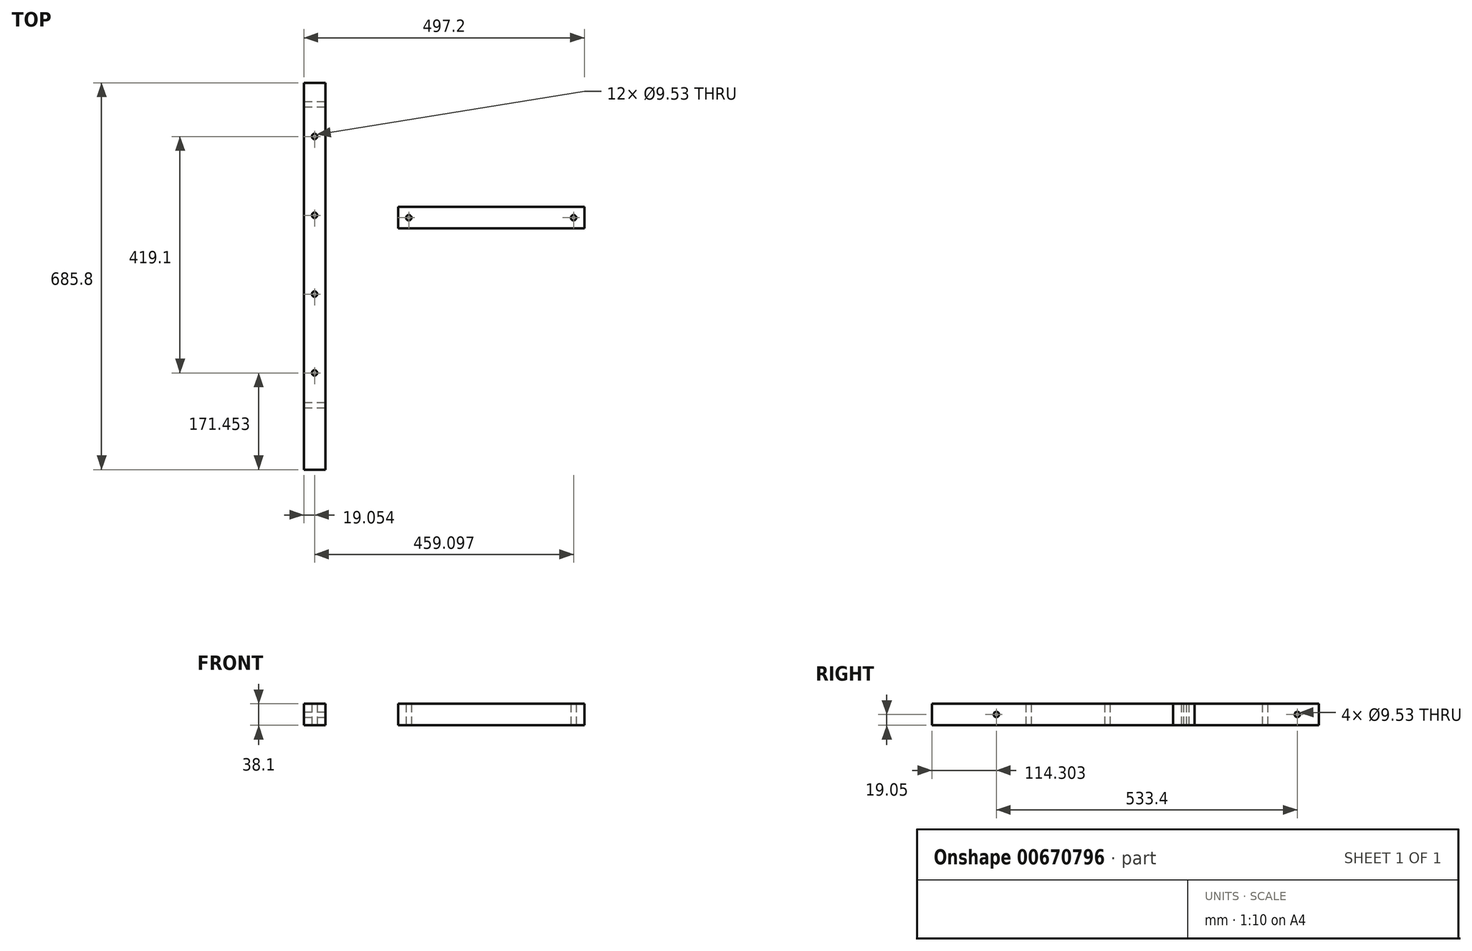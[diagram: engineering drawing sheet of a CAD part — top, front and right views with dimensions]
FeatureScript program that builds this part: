
annotation { "Feature Type Name" : "Feature", "Feature Type Description" : "" }
export const myFeature = defineFeature(function(context is Context, id is Id, definition is map)
    precondition{}
    {
        {
            var Q0;
            Q0=qCreatedBy(makeId("Top.planeOp"),FACE);
            var sketch = newSketch(context, id + "F0", { "sketchPlane" : qUnion([Q0])});
            skLineSegment(sketch, "E0.bottom", {"start": v(-17.74, 378.87) * mm, "end": v(20.36, 378.87) * mm});
            skLineSegment(sketch, "E0.top", {"start": v(-17.74, -306.93) * mm, "end": v(20.36, -306.93) * mm});
            skLineSegment(sketch, "E0.left", {"start": v(-17.74, 378.87) * mm, "end": v(-17.74, -306.93) * mm});
            skLineSegment(sketch, "E0.right", {"start": v(20.36, 378.87) * mm, "end": v(20.36, -306.93) * mm});
            skSolve(sketch);
        }
        {
            var Q0;
            Q0=makeQuery(id+"F0.imprint","IMPRINT",FACE,{"disambiguationData":[TD([[makeQuery(id+"F0.imprint","IMPRINT",EDGE,{"derivedFrom":sQuery(id+"F0.wireOp",EDGE,"E0.bottom")}),-1.0]])]});
            var Q1;
            Q1 = qSketchRegion(id + "F2", true);
            extrude(context, id + "F1", {"entities" : qUnion([Q0, Q1]), "depth" : 38.1 * mm, "offsetDistance" : 25.4 * mm});
        }
        {
            var Q0;
            Q0=makeQuery(id+"F1.opExtrude","CAP_FACE",FACE,{"disambiguationData":[OSD([sQuery(id+"F0.wireOp",EDGE,"E0.bottom"),sQuery(id+"F0.wireOp",EDGE,"E0.top"),sQuery(id+"F0.wireOp",EDGE,"E0.left"),sQuery(id+"F0.wireOp",EDGE,"E0.right")])],"isStart":true});
            var sketch = newSketch(context, id + "F2", { "sketchPlane" : qUnion([Q0])});
            skPoint(sketch, "E1", {"position": v(1.31, -283.62) * mm});
            skPoint(sketch, "E2", {"position": v(1.31, -143.92) * mm});
            skPoint(sketch, "E3", {"position": v(1.31, -4.22) * mm});
            skPoint(sketch, "E4", {"position": v(1.31, 135.48) * mm});
            skSolve(sketch);
        }
        {
            var Q0;
            Q0=makeQuery(id+"F1.opExtrude","SWEPT_FACE",FACE,{"disambiguationData":[OSD([sQuery(id+"F0.wireOp",EDGE,"E0.right")])]});
            var sketch = newSketch(context, id + "F3", { "sketchPlane" : qUnion([Q0])});
            skPoint(sketch, "E5", {"position": v(-192.63, 19.05) * mm});
            skPoint(sketch, "E6", {"position": v(340.77, 19.05) * mm});
            skSolve(sketch);
        }
        {
            var Q0;
            Q0=sQuery(id+"F2.wireOp",VERTEX,"a3873a67-aabc-4409-9fdf-016a4dbcbf0b");
            var Q1;
            Q1=sQuery(id+"F2.wireOp",VERTEX,"E4");
            var Q2;
            Q2=makeQuery(id+"F1.opExtrude","SWEPT_BODY",BODY,{"disambiguationData":[OSD([sQuery(id+"F0.wireOp",EDGE,"E0.bottom"),sQuery(id+"F0.wireOp",EDGE,"E0.top"),sQuery(id+"F0.wireOp",EDGE,"E0.left"),sQuery(id+"F0.wireOp",EDGE,"E0.right")])]});
            hole(context, id + "F4", {"style" : HoleStyle.SIMPLE, "endStyle" : HoleEndStyle.THROUGH, "holeDiameter" : 9.52 * mm, "majorDiameter" : 6.35 * mm, "isTappedThrough" : true, "tappedDepth" : 12.7 * mm, "tapClearance" : 3, "startFromSketch" : true, "locations" : qUnion([Q0, Q1]), "scope" : qUnion([Q2])});
        }
        {
            var Q0;
            Q0=sQuery(id+"F2.wireOp",VERTEX,"83af786d-4d35-481f-8a64-2c29215b7ae6");
            var Q1;
            Q1=sQuery(id+"F2.wireOp",VERTEX,"E3");
            var Q2;
            Q2=makeQuery(id+"F1.opExtrude","SWEPT_BODY",BODY,{"disambiguationData":[OSD([sQuery(id+"F0.wireOp",EDGE,"E0.bottom"),sQuery(id+"F0.wireOp",EDGE,"E0.top"),sQuery(id+"F0.wireOp",EDGE,"E0.left"),sQuery(id+"F0.wireOp",EDGE,"E0.right")])]});
            hole(context, id + "F5", {"style" : HoleStyle.SIMPLE, "endStyle" : HoleEndStyle.THROUGH, "holeDiameter" : 9.52 * mm, "majorDiameter" : 6.35 * mm, "isTappedThrough" : true, "tappedDepth" : 12.7 * mm, "tapClearance" : 3, "startFromSketch" : true, "locations" : qUnion([Q0, Q1]), "scope" : qUnion([Q2])});
        }
        {
            var Q0;
            Q0=sQuery(id+"F2.wireOp",VERTEX,"d702d4f4-6dca-422e-905c-935ee7591422");
            var Q1;
            Q1=sQuery(id+"F2.wireOp",VERTEX,"E2");
            var Q2;
            Q2=makeQuery(id+"F1.opExtrude","SWEPT_BODY",BODY,{"disambiguationData":[OSD([sQuery(id+"F0.wireOp",EDGE,"E0.bottom"),sQuery(id+"F0.wireOp",EDGE,"E0.top"),sQuery(id+"F0.wireOp",EDGE,"E0.left"),sQuery(id+"F0.wireOp",EDGE,"E0.right")])]});
            hole(context, id + "F6", {"style" : HoleStyle.SIMPLE, "endStyle" : HoleEndStyle.THROUGH, "holeDiameter" : 9.52 * mm, "majorDiameter" : 6.35 * mm, "isTappedThrough" : true, "tappedDepth" : 12.7 * mm, "tapClearance" : 3, "startFromSketch" : true, "locations" : qUnion([Q0, Q1]), "scope" : qUnion([Q2])});
        }
        {
            var Q0;
            Q0=sQuery(id+"F2.wireOp",VERTEX,"E1");
            var Q1;
            Q1=makeQuery(id+"F1.opExtrude","SWEPT_BODY",BODY,{"disambiguationData":[OSD([sQuery(id+"F0.wireOp",EDGE,"E0.bottom"),sQuery(id+"F0.wireOp",EDGE,"E0.top"),sQuery(id+"F0.wireOp",EDGE,"E0.left"),sQuery(id+"F0.wireOp",EDGE,"E0.right")])]});
            hole(context, id + "F7", {"style" : HoleStyle.SIMPLE, "endStyle" : HoleEndStyle.THROUGH, "holeDiameter" : 9.52 * mm, "majorDiameter" : 6.35 * mm, "isTappedThrough" : true, "tappedDepth" : 12.7 * mm, "tapClearance" : 3, "startFromSketch" : true, "locations" : qUnion([Q0]), "scope" : qUnion([Q1])});
        }
        {
            var Q0;
            Q0=sQuery(id+"F3.wireOp",VERTEX,"E5");
            var Q1;
            Q1=makeQuery(id+"F1.opExtrude","SWEPT_BODY",BODY,{"disambiguationData":[OSD([sQuery(id+"F0.wireOp",EDGE,"E0.bottom"),sQuery(id+"F0.wireOp",EDGE,"E0.top"),sQuery(id+"F0.wireOp",EDGE,"E0.left"),sQuery(id+"F0.wireOp",EDGE,"E0.right")])]});
            hole(context, id + "F8", {"style" : HoleStyle.SIMPLE, "endStyle" : HoleEndStyle.THROUGH, "holeDiameter" : 9.52 * mm, "majorDiameter" : 6.35 * mm, "isTappedThrough" : true, "tappedDepth" : 12.7 * mm, "tapClearance" : 3, "startFromSketch" : true, "locations" : qUnion([Q0]), "scope" : qUnion([Q1])});
        }
        {
            var Q0;
            Q0=sQuery(id+"F3.wireOp",VERTEX,"E6");
            var Q1;
            Q1=makeQuery(id+"F1.opExtrude","SWEPT_BODY",BODY,{"disambiguationData":[OSD([sQuery(id+"F0.wireOp",EDGE,"E0.bottom"),sQuery(id+"F0.wireOp",EDGE,"E0.top"),sQuery(id+"F0.wireOp",EDGE,"E0.left"),sQuery(id+"F0.wireOp",EDGE,"E0.right")])]});
            hole(context, id + "F9", {"style" : HoleStyle.SIMPLE, "endStyle" : HoleEndStyle.THROUGH, "holeDiameter" : 9.52 * mm, "majorDiameter" : 6.35 * mm, "isTappedThrough" : true, "tappedDepth" : 12.7 * mm, "tapClearance" : 3, "startFromSketch" : true, "locations" : qUnion([Q0]), "scope" : qUnion([Q1])});
        }
        {
            var Q0;
            Q0=qCreatedBy(makeId("Top.planeOp"),FACE);
            var sketch = newSketch(context, id + "F10", { "sketchPlane" : qUnion([Q0])});
            skLineSegment(sketch, "E7.bottom", {"start": v(149.26, 158.68) * mm, "end": v(479.46, 158.68) * mm});
            skLineSegment(sketch, "E7.top", {"start": v(149.26, 120.58) * mm, "end": v(479.46, 120.58) * mm});
            skLineSegment(sketch, "E7.left", {"start": v(149.26, 158.68) * mm, "end": v(149.26, 120.58) * mm});
            skLineSegment(sketch, "E7.right", {"start": v(479.46, 158.68) * mm, "end": v(479.46, 120.58) * mm});
            skPoint(sketch, "E8", {"position": v(168.31, 139.63) * mm});
            skPoint(sketch, "E9", {"position": v(460.41, 139.63) * mm});
            skSolve(sketch);
        }
        {
            var Q0;
            Q0 = qSketchRegion(id + "F10", true);
            extrude(context, id + "F11", {"entities" : qUnion([Q0]), "depth" : 38.1 * mm, "offsetDistance" : 25.4 * mm});
        }
        {
            var Q0;
            Q0=sQuery(id+"F10.wireOp",VERTEX,"E8");
            var Q1;
            Q1=makeQuery(id+"F11.opExtrude","SWEPT_BODY",BODY,{"disambiguationData":[OSD([sQuery(id+"F10.wireOp",EDGE,"E7.bottom"),sQuery(id+"F10.wireOp",EDGE,"E7.top"),sQuery(id+"F10.wireOp",EDGE,"E7.left"),sQuery(id+"F10.wireOp",EDGE,"E7.right")])]});
            hole(context, id + "F12", {"style" : HoleStyle.SIMPLE, "endStyle" : HoleEndStyle.THROUGH, "oppositeDirection" : true, "holeDiameter" : 9.52 * mm, "majorDiameter" : 6.35 * mm, "isTappedThrough" : true, "tappedDepth" : 12.7 * mm, "tapClearance" : 3, "startFromSketch" : true, "locations" : qUnion([Q0]), "scope" : qUnion([Q1])});
        }
        {
            var Q0;
            Q0=sQuery(id+"F10.wireOp",VERTEX,"E9");
            var Q1;
            Q1=makeQuery(id+"F11.opExtrude","SWEPT_BODY",BODY,{"disambiguationData":[OSD([sQuery(id+"F10.wireOp",EDGE,"E7.bottom"),sQuery(id+"F10.wireOp",EDGE,"E7.top"),sQuery(id+"F10.wireOp",EDGE,"E7.left"),sQuery(id+"F10.wireOp",EDGE,"E7.right")])]});
            hole(context, id + "F13", {"style" : HoleStyle.SIMPLE, "endStyle" : HoleEndStyle.THROUGH, "oppositeDirection" : true, "holeDiameter" : 9.52 * mm, "majorDiameter" : 6.35 * mm, "isTappedThrough" : true, "tappedDepth" : 12.7 * mm, "tapClearance" : 3, "startFromSketch" : true, "locations" : qUnion([Q0]), "scope" : qUnion([Q1])});
        }
    });
